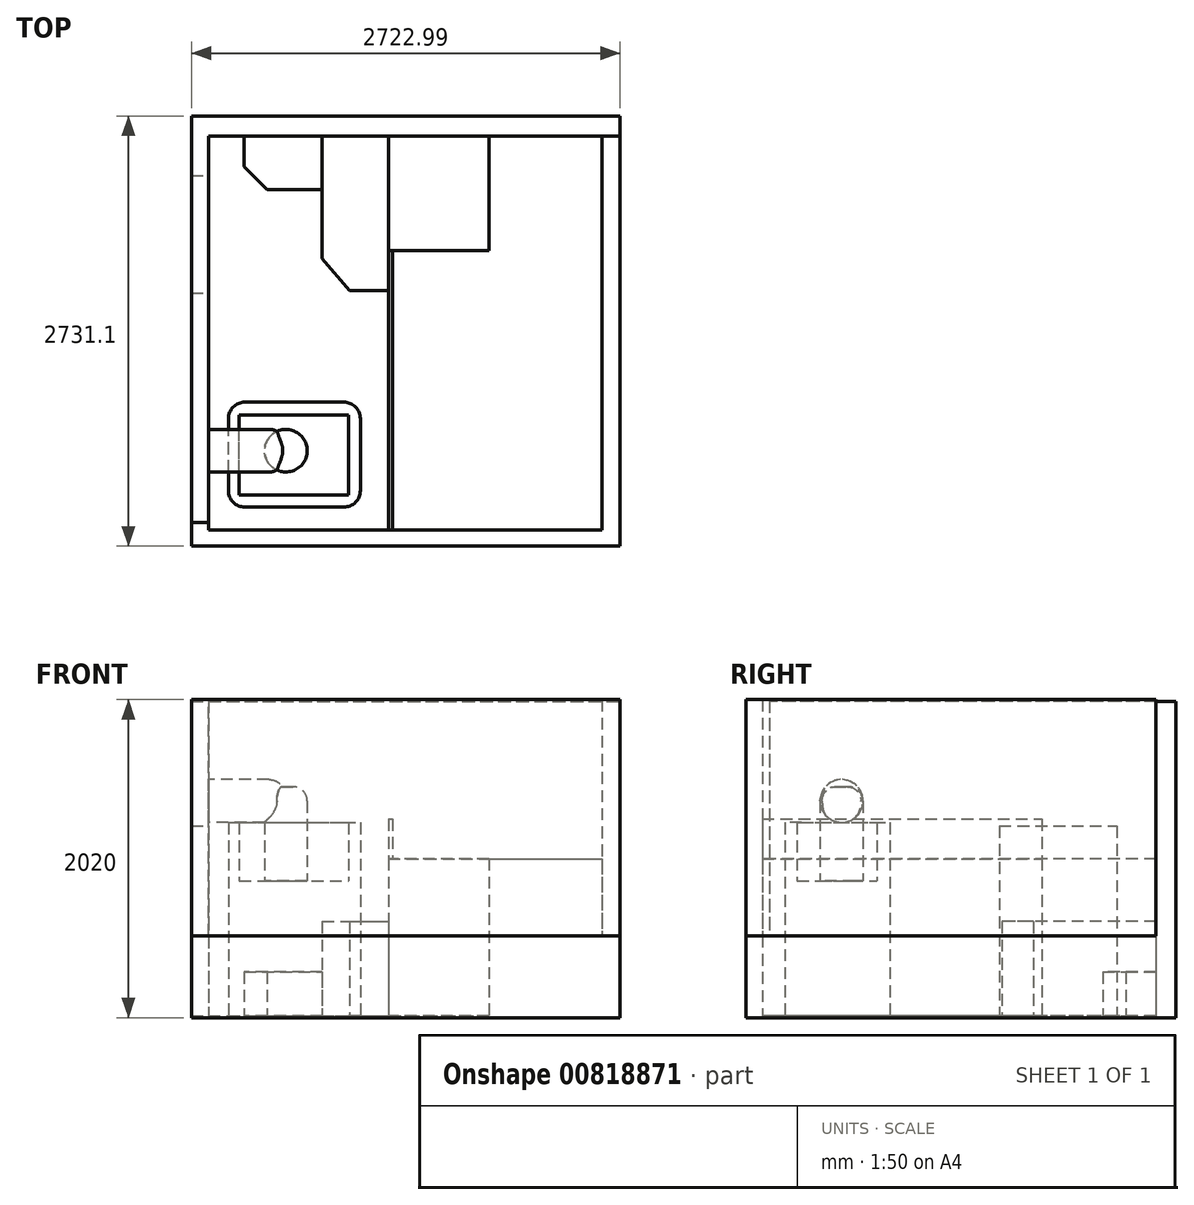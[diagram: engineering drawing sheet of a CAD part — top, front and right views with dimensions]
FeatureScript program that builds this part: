
annotation { "Feature Type Name" : "Feature", "Feature Type Description" : "" }
export const myFeature = defineFeature(function(context is Context, id is Id, definition is map)
    precondition{}
    {
        {
            var Q0;
            Q0=qCreatedBy(makeId("Top.planeOp"),FACE);
            var sketch = newSketch(context, id + "F0", { "sketchPlane" : qUnion([Q0])});
            skLineSegment(sketch, "E0.bottom", {"start": v(-1248.5, 1360.59) * mm, "end": v(1251.5, 1360.59) * mm});
            skLineSegment(sketch, "E0.top", {"start": v(-1248.5, -1139.41) * mm, "end": v(1251.5, -1139.41) * mm});
            skLineSegment(sketch, "E0.left", {"start": v(-1248.5, 1360.59) * mm, "end": v(-1248.5, -1139.41) * mm});
            skLineSegment(sketch, "E0.right", {"start": v(1251.5, 1360.59) * mm, "end": v(1251.5, -1139.41) * mm});
            skLineSegment(sketch, "E1.bottom", {"start": v(-1356.71, 1488.25) * mm, "end": v(1366.28, 1488.25) * mm});
            skLineSegment(sketch, "E1.top", {"start": v(-1356.71, -1242.85) * mm, "end": v(1366.28, -1242.85) * mm});
            skLineSegment(sketch, "E1.left", {"start": v(-1356.71, 1488.25) * mm, "end": v(-1356.71, -1242.85) * mm});
            skLineSegment(sketch, "E1.right", {"start": v(1366.28, 1488.25) * mm, "end": v(1366.28, -1242.85) * mm});
            skSolve(sketch);
        }
        {
            var Q0;
            Q0=makeQuery(id+"F0.imprint","IMPRINT",FACE,{"disambiguationData":[TD([[makeQuery(id+"F0.imprint","IMPRINT",EDGE,{"derivedFrom":sQuery(id+"F0.wireOp",EDGE,"E0.bottom")}),1.0]])]});
            extrude(context, id + "F1", {"entities" : qUnion([Q0]), "depth" : 2010 * mm, "offsetDistance" : 25 * mm});
        }
        {
            var Q0;
            Q0=makeQuery(id+"F1.opExtrude","SWEPT_FACE",FACE,{"disambiguationData":[OSD([sQuery(id+"F0.wireOp",EDGE,"E0.right")])]});
            extrude(context, id + "F2", {"entities" : qUnion([Q0]), "operationType" : NewBodyOperationType.REMOVE, "oppositeDirection" : true, "depth" : 420 * mm, "offsetDistance" : 25 * mm});
        }
        {
            var Q0;
            Q0=makeQuery(id+"F1.opExtrude","SWEPT_FACE",FACE,{"disambiguationData":[OSD([sQuery(id+"F0.wireOp",EDGE,"E1.top")])]});
            extrude(context, id + "F3", {"entities" : qUnion([Q0]), "operationType" : NewBodyOperationType.REMOVE, "oppositeDirection" : true, "depth" : 150 * mm, "offsetDistance" : 25 * mm});
        }
        {
            var Q0;
            Q0 = qSketchRegion(id + "F0", true);
            extrude(context, id + "F4", {"entities" : qUnion([Q0]), "operationType" : NewBodyOperationType.ADD, "depth" : 520 * mm, "offsetDistance" : 25 * mm});
        }
        {
            var Q0;
            Q0=makeQuery(id+"F0.imprint","IMPRINT",FACE,{"disambiguationData":[TD([[makeQuery(id+"F0.imprint","IMPRINT",EDGE,{"derivedFrom":sQuery(id+"F0.wireOp",EDGE,"E0.bottom")}),-1.0]])]});
            extrude(context, id + "F5", {"entities" : qUnion([Q0]), "operationType" : NewBodyOperationType.ADD, "depth" : 10 * mm, "offsetDistance" : 25 * mm});
        }
        {
            var Q0;
            {var subQ0=sQuery(id+"F0.wireOp",EDGE,"E0.left");Q0=makeQuery(id+"F4.boolean.opBoolean","MERGE",FACE,{"derivedFrom":[makeQuery(id+"F1.opExtrude","SWEPT_FACE",FACE,{"disambiguationData":[OSD([subQ0])]}),makeQuery(id+"F4.opExtrude","SWEPT_FACE",FACE,{"disambiguationData":[OSD([subQ0])]})]});}
            var sketch = newSketch(context, id + "F6", { "sketchPlane" : qUnion([Q0])});
            skLineSegment(sketch, "E2.bottom", {"start": v(365.58, 1218.28) * mm, "end": v(1111.34, 1218.28) * mm});
            skLineSegment(sketch, "E2.top", {"start": v(365.58, 10) * mm, "end": v(1111.34, 10) * mm});
            skLineSegment(sketch, "E2.left", {"start": v(365.58, 1218.28) * mm, "end": v(365.58, 10) * mm});
            skLineSegment(sketch, "E2.right", {"start": v(1111.34, 1218.28) * mm, "end": v(1111.34, 10) * mm});
            skSolve(sketch);
        }
        {
            var Q0;
            Q0 = qSketchRegion(id + "F6", true);
            extrude(context, id + "F7", {"entities" : qUnion([Q0]), "operationType" : NewBodyOperationType.REMOVE, "oppositeDirection" : true, "depth" : 640 * mm, "offsetDistance" : 25 * mm});
        }
        {
            var Q0;
            Q0=makeQuery(id+"F7.boolean.opBoolean","MERGE",FACE,{"derivedFrom":[makeQuery(id+"F5.opExtrude","CAP_FACE",FACE,{"disambiguationData":[OSD([sQuery(id+"F0.wireOp",EDGE,"E0.bottom"),sQuery(id+"F0.wireOp",EDGE,"E0.top"),sQuery(id+"F0.wireOp",EDGE,"E0.left"),sQuery(id+"F0.wireOp",EDGE,"E0.right")])],"isStart":false}),makeQuery(id+"F7.opExtrude","SWEPT_FACE",FACE,{"disambiguationData":[OSD([sQuery(id+"F6.wireOp",EDGE,"E2.top")])]})]});
            var sketch = newSketch(context, id + "F8", { "sketchPlane" : qUnion([Q0])});
            skLineSegment(sketch, "E3.bottom", {"start": v(-1121, -994.76) * mm, "end": v(-283.37, -994.76) * mm});
            skLineSegment(sketch, "E3.top", {"start": v(-1121, -328.4) * mm, "end": v(-283.37, -328.4) * mm});
            skLineSegment(sketch, "E3.left", {"start": v(-1121, -994.76) * mm, "end": v(-1121, -328.4) * mm});
            skLineSegment(sketch, "E3.right", {"start": v(-283.37, -994.76) * mm, "end": v(-283.37, -328.4) * mm});
            skLineSegment(sketch, "E4.bottom", {"start": v(-1052.5, -919) * mm, "end": v(-358.4, -919) * mm});
            skLineSegment(sketch, "E4.top", {"start": v(-1052.5, -410.09) * mm, "end": v(-358.4, -410.09) * mm});
            skLineSegment(sketch, "E4.left", {"start": v(-1052.5, -919) * mm, "end": v(-1052.5, -410.09) * mm});
            skLineSegment(sketch, "E4.right", {"start": v(-358.4, -919) * mm, "end": v(-358.4, -410.09) * mm});
            skSolve(sketch);
        }
        {
            var Q0;
            Q0 = qSketchRegion(id + "F8", true);
            extrude(context, id + "F9", {"entities" : qUnion([Q0]), "operationType" : NewBodyOperationType.ADD, "depth" : 1230 * mm, "offsetDistance" : 25 * mm});
        }
        {
            var Q0;
            Q0=makeQuery(id+"F9.boolean.opBoolean","SPLIT",FACE,{"disambiguationData":[TD([makeQuery(id+"F9.opExtrude","SWEPT_FACE",FACE,{"disambiguationData":[OSD([sQuery(id+"F8.wireOp",EDGE,"E4.bottom")])]})])],"derivedFrom":makeQuery(id+"F7.boolean.opBoolean","MERGE",FACE,{"derivedFrom":[makeQuery(id+"F5.opExtrude","CAP_FACE",FACE,{"disambiguationData":[OSD([sQuery(id+"F0.wireOp",EDGE,"E0.bottom"),sQuery(id+"F0.wireOp",EDGE,"E0.top"),sQuery(id+"F0.wireOp",EDGE,"E0.left"),sQuery(id+"F0.wireOp",EDGE,"E0.right")])],"isStart":false}),makeQuery(id+"F7.opExtrude","SWEPT_FACE",FACE,{"disambiguationData":[OSD([sQuery(id+"F6.wireOp",EDGE,"E2.top")])]})]})});
            extrude(context, id + "F10", {"entities" : qUnion([Q0]), "operationType" : NewBodyOperationType.ADD, "depth" : 860 * mm, "offsetDistance" : 25 * mm});
        }
        {
            var Q0;
            Q0=makeQuery(id+"F9.opExtrude","SWEPT_EDGE",EDGE,{"disambiguationData":[OSD([sQuery(id+"F8.wireOp",EDGE,"E3.bottom"),sQuery(id+"F8.wireOp",EDGE,"E3.right")])]});
            var Q1;
            Q1=makeQuery(id+"F9.opExtrude","SWEPT_EDGE",EDGE,{"disambiguationData":[OSD([sQuery(id+"F8.wireOp",EDGE,"E3.top"),sQuery(id+"F8.wireOp",EDGE,"E3.right")])]});
            var Q2;
            Q2=makeQuery(id+"F9.opExtrude","SWEPT_EDGE",EDGE,{"disambiguationData":[OSD([sQuery(id+"F8.wireOp",EDGE,"E3.top"),sQuery(id+"F8.wireOp",EDGE,"E3.left")])]});
            var Q3;
            Q3=makeQuery(id+"F9.opExtrude","SWEPT_EDGE",EDGE,{"disambiguationData":[OSD([sQuery(id+"F8.wireOp",EDGE,"E3.bottom"),sQuery(id+"F8.wireOp",EDGE,"E3.left")])]});
            fillet(context, id + "F11", {"entities" : qUnion([Q0, Q1, Q2, Q3]), "radius" : 105 * mm, "tangentPropagation" : true, "allowEdgeOverflow" : false});
        }
        {
            var Q0;
            {var subQ1=sQuery(id+"F0.wireOp",EDGE,"E0.right");var subQ2=sQuery(id+"F0.wireOp",EDGE,"E0.left");var subQ3=sQuery(id+"F0.wireOp",EDGE,"E0.top");var subQ4=sQuery(id+"F0.wireOp",EDGE,"E0.bottom");Q0=makeQuery(id+"F9.boolean.opBoolean","SPLIT",FACE,{"disambiguationData":[TD([makeQuery(id+"F1.opExtrude","SWEPT_FACE",FACE,{"disambiguationData":[OSD([subQ4])]})])],"derivedFrom":makeQuery(id+"F7.boolean.opBoolean","MERGE",FACE,{"derivedFrom":[makeQuery(id+"F5.opExtrude","CAP_FACE",FACE,{"disambiguationData":[OSD([subQ4,subQ3,subQ2,subQ1])],"isStart":false}),makeQuery(id+"F7.opExtrude","SWEPT_FACE",FACE,{"disambiguationData":[OSD([sQuery(id+"F6.wireOp",EDGE,"E2.top")])]})]})});}
            var sketch = newSketch(context, id + "F12", { "sketchPlane" : qUnion([Q0])});
            skLineSegment(sketch, "E5.bottom", {"start": v(533.18, 1360.59) * mm, "end": v(1251.5, 1360.59) * mm});
            skLineSegment(sketch, "E5.top", {"start": v(533.18, -1139.41) * mm, "end": v(1251.5, -1139.41) * mm});
            skLineSegment(sketch, "E5.left", {"start": v(533.18, 1360.59) * mm, "end": v(533.18, -1139.41) * mm});
            skLineSegment(sketch, "E5.right", {"start": v(1251.5, 1360.59) * mm, "end": v(1251.5, -1139.41) * mm});
            skLineSegment(sketch, "E6.bottom", {"start": v(533.18, 635.54) * mm, "end": v(-104.7, 635.54) * mm});
            skLineSegment(sketch, "E6.top", {"start": v(533.18, -1139.41) * mm, "end": v(-104.7, -1139.41) * mm});
            skLineSegment(sketch, "E6.left", {"start": v(533.18, 635.54) * mm, "end": v(533.18, -1139.41) * mm});
            skLineSegment(sketch, "E6.right", {"start": v(-104.7, 635.54) * mm, "end": v(-104.7, -1139.41) * mm});
            skLineSegment(sketch, "E7.bottom", {"start": v(-104.7, 1360.59) * mm, "end": v(533.18, 1360.59) * mm});
            skLineSegment(sketch, "E7.top", {"start": v(-104.7, 635.54) * mm, "end": v(533.18, 635.54) * mm});
            skLineSegment(sketch, "E7.left", {"start": v(-104.7, 1360.59) * mm, "end": v(-104.7, 635.54) * mm});
            skLineSegment(sketch, "E7.right", {"start": v(533.18, 1360.59) * mm, "end": v(533.18, 635.54) * mm});
            skLineSegment(sketch, "E8.right", {"start": v(-104.7, 1360.59) * mm, "end": v(-104.7, 998.06) * mm});
            skLineSegment(sketch, "E9", {"start": v(-525.53, 1360.59) * mm, "end": v(-525.53, 583.2) * mm});
            skLineSegment(sketch, "E10", {"start": v(-525.53, 583.2) * mm, "end": v(-352.9, 381.8) * mm});
            skLineSegment(sketch, "E11", {"start": v(-352.9, 381.8) * mm, "end": v(-104.7, 381.8) * mm});
            skLineSegment(sketch, "E12", {"start": v(-525.53, 1021.96) * mm, "end": v(-874.38, 1021.96) * mm});
            skLineSegment(sketch, "E13", {"start": v(-874.38, 1021.96) * mm, "end": v(-1021.83, 1169.4) * mm});
            skLineSegment(sketch, "E14", {"start": v(-1021.83, 1169.4) * mm, "end": v(-1021.83, 1360.59) * mm});
            skSolve(sketch);
        }
        {
            var Q0;
            Q0=makeQuery(id+"F12.imprint","IMPRINT",FACE,{"disambiguationData":[TD([[makeQuery(id+"F12.imprint","IMPRINT",EDGE,{"derivedFrom":sQuery(id+"F12.wireOp",EDGE,"E5.bottom")}),-1.0]])]});
            var Q1;
            Q1=makeQuery(id+"F12.imprint","IMPRINT",FACE,{"disambiguationData":[TD([[makeQuery(id+"F12.imprint","IMPRINT",EDGE,{"derivedFrom":sQuery(id+"F12.wireOp",EDGE,"E6.top")}),1.0]])]});
            var Q2;
            Q2=sQuery(id+"F12.wireOp",EDGE,"E5.left");
            extrude(context, id + "F13", {"entities" : qUnion([Q0, Q1]), "operationType" : NewBodyOperationType.ADD, "surfaceEntities" : qUnion([Q2]), "depth" : 1000 * mm, "offsetDistance" : 25 * mm});
        }
        {
            var Q0;
            Q0=makeQuery(id+"F12.imprint","IMPRINT",FACE,{"disambiguationData":[TD([[makeQuery(id+"F12.imprint","IMPRINT",EDGE,{"derivedFrom":sQuery(id+"F12.wireOp",EDGE,"E7.bottom")}),-1.0]])]});
            extrude(context, id + "F14", {"entities" : qUnion([Q0]), "depth" : 1000 * mm, "offsetDistance" : 25 * mm});
        }
        {
            var Q0;
            {var subQ5=sQuery(id+"F12.wireOp",EDGE,"E7.left");Q0=makeQuery(id+"F12.imprint","IMPRINT",FACE,{"disambiguationData":[TD([[makeQuery(id+"F12.imprint","IMPRINT",EDGE,{"derivedFrom":subQ5}),-1.0]])]});}
            extrude(context, id + "F15", {"entities" : qUnion([Q0]), "depth" : 600 * mm, "offsetDistance" : 25 * mm});
        }
        {
            var Q0;
            {var subQ1=sQuery(id+"F12.wireOp",EDGE,"E12");Q0=makeQuery(id+"F12.imprint","IMPRINT",FACE,{"disambiguationData":[TD([[makeQuery(id+"F12.imprint","IMPRINT",EDGE,{"derivedFrom":subQ1}),-1.0]])]});}
            extrude(context, id + "F16", {"entities" : qUnion([Q0]), "depth" : 280 * mm, "offsetDistance" : 25 * mm});
        }
        {
            var Q0;
            Q0=makeQuery(id+"F13.opExtrude","CAP_FACE",FACE,{"disambiguationData":[OSD([sQuery(id+"F12.wireOp",EDGE,"E5.bottom"),sQuery(id+"F12.wireOp",EDGE,"E5.top"),sQuery(id+"F12.wireOp",EDGE,"E5.right"),sQuery(id+"F12.wireOp",EDGE,"E6.top"),sQuery(id+"F12.wireOp",EDGE,"E6.right"),sQuery(id+"F12.wireOp",EDGE,"E7.top"),sQuery(id+"F12.wireOp",EDGE,"E7.right")])],"isStart":false});
            var sketch = newSketch(context, id + "F17", { "sketchPlane" : qUnion([Q0])});
            skLineSegment(sketch, "E15", {"start": v(-104.7, 635.54) * mm, "end": v(-104.7, -1139.41) * mm});
            skLineSegment(sketch, "E16", {"start": v(-104.7, -1139.41) * mm, "end": v(-79.97, -1139.41) * mm});
            skLineSegment(sketch, "E17", {"start": v(-79.97, -1139.41) * mm, "end": v(-79.97, 635.54) * mm});
            skLineSegment(sketch, "E18", {"start": v(-79.97, 635.54) * mm, "end": v(-104.7, 635.54) * mm});
            skSolve(sketch);
        }
        {
            var Q0;
            Q0=makeQuery(id+"F17.imprint","IMPRINT",FACE,{"disambiguationData":[TD([[makeQuery(id+"F17.imprint","IMPRINT",EDGE,{"derivedFrom":sQuery(id+"F17.wireOp",EDGE,"E15")}),1.0]])]});
            extrude(context, id + "F18", {"entities" : qUnion([Q0]), "depth" : 252 * mm, "offsetDistance" : 25 * mm});
        }
        {
            var Q0;
            Q0=makeQuery(id+"F4.opExtrude","CAP_FACE",FACE,{"disambiguationData":[OSD([sQuery(id+"F0.wireOp",EDGE,"E0.bottom"),sQuery(id+"F0.wireOp",EDGE,"E0.top"),sQuery(id+"F0.wireOp",EDGE,"E0.left"),sQuery(id+"F0.wireOp",EDGE,"E0.right"),sQuery(id+"F0.wireOp",EDGE,"E1.bottom"),sQuery(id+"F0.wireOp",EDGE,"E1.top"),sQuery(id+"F0.wireOp",EDGE,"E1.left"),sQuery(id+"F0.wireOp",EDGE,"E1.right")])],"isStart":false});
            extrude(context, id + "F19", {"entities" : qUnion([Q0]), "depth" : 1500 * mm, "offsetDistance" : 25 * mm});
        }
        {
            var Q0;
            {var subQ0=sQuery(id+"F0.wireOp",EDGE,"E0.left");Q0=makeQuery(id+"F4.boolean.opBoolean","MERGE",FACE,{"derivedFrom":[makeQuery(id+"F1.opExtrude","SWEPT_FACE",FACE,{"disambiguationData":[OSD([subQ0])]}),makeQuery(id+"F4.opExtrude","SWEPT_FACE",FACE,{"disambiguationData":[OSD([subQ0])]})]});}
            var sketch = newSketch(context, id + "F20", { "sketchPlane" : qUnion([Q0])});
            skCircle(sketch, "E19", {"center": v(-636.4, 1376.36) * mm, "radius": 135.83 * mm});
            skSolve(sketch);
        }
        {
            var Q0;
            Q0 = qSketchRegion(id + "F20", true);
            extrude(context, id + "F21", {"entities" : qUnion([Q0]), "operationType" : NewBodyOperationType.ADD, "depth" : 490 * mm, "offsetDistance" : 25 * mm});
        }
        {
            var Q0;
            Q0=makeQuery(id+"F10.opExtrude","CAP_FACE",FACE,{"disambiguationData":[OSD([sQuery(id+"F0.wireOp",EDGE,"E0.bottom"),sQuery(id+"F0.wireOp",EDGE,"E0.top"),sQuery(id+"F0.wireOp",EDGE,"E0.left"),sQuery(id+"F0.wireOp",EDGE,"E0.right"),sQuery(id+"F6.wireOp",EDGE,"E2.top")])],"isStart":false});
            var sketch = newSketch(context, id + "F22", { "sketchPlane" : qUnion([Q0])});
            skCircle(sketch, "E20", {"center": v(-756.9, -636.59) * mm, "radius": 135.44 * mm});
            skSolve(sketch);
        }
        {
            var Q0;
            Q0 = qSketchRegion(id + "F22", true);
            extrude(context, id + "F23", {"entities" : qUnion([Q0]), "operationType" : NewBodyOperationType.ADD, "depth" : 596 * mm, "offsetDistance" : 25 * mm});
        }
        {
            var Q0;
            {var subQ0=sQuery(id+"F20.wireOp",EDGE,"E19");Q0=makeQuery(id+"F23.boolean.opBoolean","SPLIT",EDGE,{"disambiguationData":[TD([makeQuery(id+"F21.opExtrude","SWEPT_FACE",FACE,{"disambiguationData":[OSD([subQ0])]}),makeQuery(id+"F21.opExtrude","CAP_FACE",FACE,{"disambiguationData":[OSD([subQ0])],"isStart":false}),makeQuery(id+"F23.opExtrude","CAP_FACE",FACE,{"disambiguationData":[OSD([sQuery(id+"F22.wireOp",EDGE,"E20")])],"isStart":false})])],"derivedFrom":makeQuery(id+"F21.opExtrude","CAP_EDGE",EDGE,{"disambiguationData":[OSD([subQ0])],"isStart":false})});}
            fillet(context, id + "F24", {"entities" : qUnion([Q0]), "radius" : 105 * mm, "tangentPropagation" : true, "allowEdgeOverflow" : false});
        }
        {
            var Q0;
            Q0=makeQuery(id+"F23.opExtrude","CAP_EDGE",EDGE,{"disambiguationData":[OSD([sQuery(id+"F22.wireOp",EDGE,"E20")])],"isStart":false});
            fillet(context, id + "F25", {"entities" : qUnion([Q0]), "radius" : 89.33 * mm, "tangentPropagation" : true, "allowEdgeOverflow" : false});
        }
    });
